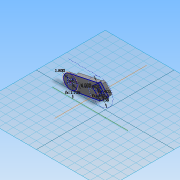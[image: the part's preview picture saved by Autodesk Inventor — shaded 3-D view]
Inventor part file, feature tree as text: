
AUTODESK INVENTOR PART (.ipt)
format: ipt  version: 2014 SP2 (Build 180246200, 246)  size: 660,992 bytes
history: native  units: in
note: dims shown in document units (in); Inventor stores cm internally (conversion verified against a paired STEP export)
features: other x28, extrude x4, fillet x4, sketch x4, hole x2
ambient origin geometry x8: Origin, YZ Plane, XZ Plane, XY Plane, X Axis, Y Axis, Z Axis, Center Point
bodies: Solid1 (feature_tree), Solid2 (feature_tree), Solid3 (feature_tree), Solid4 (feature_tree)
feature tree (42):
  other  "Truck Caliber50 9in.iam"
  other  "Baseplate Caliber50 9in.ipt:1"
  other  "Hanger Caliber50 9in.ipt:1"
  other  "Generic Riser.ipt:1"
  other  "Blocks"
  other  "Projected Axle"
  extrude  "Base"  Depth=0.3937in
  other  "Motor Holes Sketch"
  extrude  "Motor Holes"  Depth=0.3125in
  extrude  "Motor Screw Cbore"  Depth=0.3365in
  other  "Back Plane"
  extrude  "Pocket"  Depth=0.09in
  other  "Midplane"
  fillet  "Fillet1"  Radius=0.3125in
  hole  "SetScrew1"  [1 undecoded]
  hole  "SetScrew2"  [1 undecoded]
  fillet  "Fillet2"  Radius=0.4in
  fillet  "Fillet3"  Radius=0.4in
  fillet  "Fillet4"  [1 undecoded]
  other  "Work Axis1"
  other  "Work Axis2"
  other  "Work Axis3"
  other  "Vertical Axis"
  other  "Axle Axis"
  other  "Kingpin Axis"
  other  "Work Point1"
  other  "Axle"
  sketch  "Sketch1"  dims[d0=0.3937in d69=0.9843in]
  other  "Motor Attachment Block"
  other  "adjustability"
  other  "Base Sketch"
  other  "the Axle"
  other  "motor"
  other  "Motor Adjust Slots"
  sketch  "Sketch12"  dims[d74=0.5in d78=0.3125in]
  other  "TheMotor"
  sketch  "Sketch13"  dims[d79=0.71in d80=0.3365in]
  sketch  "Sketch14"  dims[d81=0.4435in d82=2.5961in d83=0.3125in d84=0.71in d85=0.9482in d87=0.4435in d88=0.3365in d97=0.4in d98=0.4in d99=0.4in d111=15.0deg d113=4.0917in d116=0.0in d119=0.1732in d120=0.1732in d121=0.1732in d127=0.1772in d128=0.1772in d129=0.1772in d130=0.5in d131=0.0in d133=0.0in d134=-0.5in d135=0.3125in d136=0.0in d144=15.0deg d146=1.7354in d153=0.25in d155=0.125in d156=0.05in d157=1.8in d158=0.25in d168=0.337in d160=0.104in d161=0.75in d162=0.375in d163=0.25in d164=0.5635in d165=1.0in d166=0.8108in d167=-0.25in d169=0.104in d170=0.75in d171=0.375in d172=0.25in d173=0.5635in d174=1.0in d175=0.8108in d176=0.3in d177=0.3in d178=0.3in d179=0.6323in d180=0.6323in d181=0.25in d182=0.125in d183=0.25in d184=0.25in d186=0.612in d187=0.612in d188=0.09in d189=0.9843in]
  other  "AxleOutline"
  other  "MotorHoles"
  other  "TheMotor:1"
  other  "TheMotor:2"
note: 3 required parameter values undecoded (feature->parameter linkage not recoverable at this tier; creation-order binding heuristic only, values carry confidence <= 0.55)
